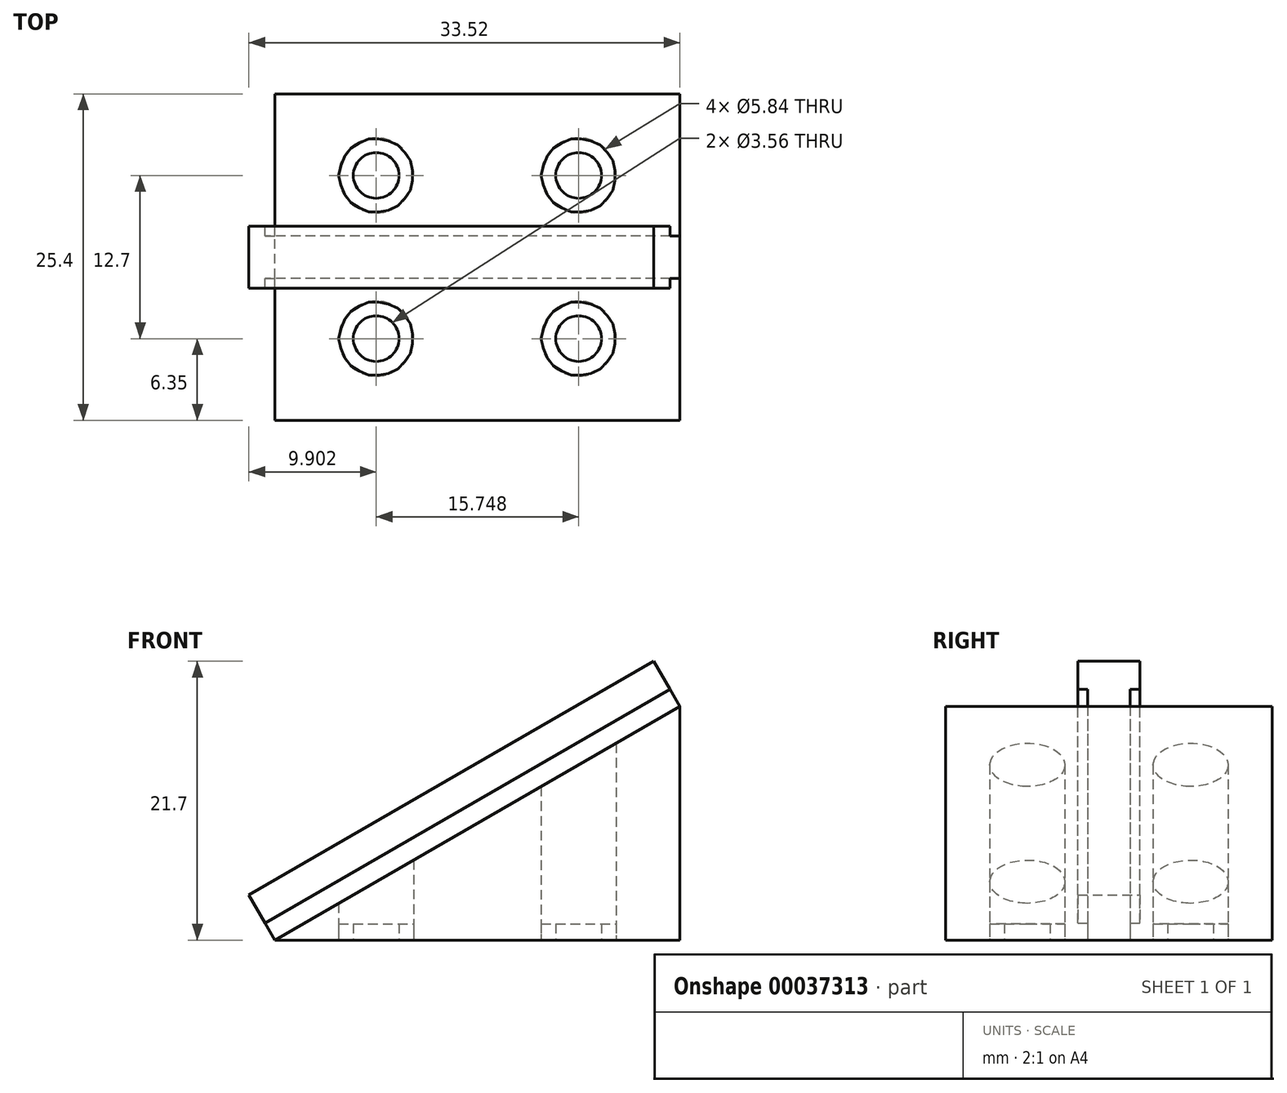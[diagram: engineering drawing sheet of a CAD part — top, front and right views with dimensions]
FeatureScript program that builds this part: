
annotation { "Feature Type Name" : "Feature", "Feature Type Description" : "" }
export const myFeature = defineFeature(function(context is Context, id is Id, definition is map)
    precondition{}
    {
        {
            var Q0;
            Q0=qCreatedBy(makeId("Front.planeOp"),FACE);
            var sketch = newSketch(context, id + "F0", { "sketchPlane" : qUnion([Q0])});
            skLineSegment(sketch, "E0", {"start": v(-14.92, 0) * mm, "end": v(16.57, 0) * mm});
            skLineSegment(sketch, "E1", {"start": v(-14.92, 0) * mm, "end": v(17.55, 18.75) * mm});
            skLineSegment(sketch, "E2", {"start": v(16.57, 0) * mm, "end": v(16.57, 18.18) * mm});
            skLineSegment(sketch, "E3", {"start": v(16.57, 18.18) * mm, "end": v(17.55, 18.75) * mm});
            skSolve(sketch);
        }
        {
            var Q0;
            Q0 = qSketchRegion(id + "F0", true);
            extrude(context, id + "F1", {"entities" : qUnion([Q0]), "depth" : 25.4 * mm});
        }
        {
            var Q0;
            Q0=makeQuery(id+"F1.opExtrude","SWEPT_FACE",FACE,{"disambiguationData":[OSD([sQuery(id+"F0.wireOp",EDGE,"E0")])]});
            var sketch = newSketch(context, id + "F2", { "sketchPlane" : qUnion([Q0])});
            skPoint(sketch, "E4.start.orphan", {"position": v(0.83, 0) * mm});
            skPoint(sketch, "E5.trimOffspring.end.orphan", {"position": v(0.83, 25.4) * mm});
            skCircle(sketch, "E6", {"center": v(-7.05, 19.05) * mm, "radius": 1.78 * mm});
            skCircle(sketch, "E7", {"center": v(-7.05, 19.05) * mm, "radius": 2.92 * mm});
            skCircle(sketch, "E8.MirrorC", {"center": v(8.7, 19.05) * mm, "radius": 1.78 * mm});
            skCircle(sketch, "E9.MirrorC", {"center": v(8.7, 19.05) * mm, "radius": 2.92 * mm});
            skPoint(sketch, "E10.orphan", {"position": v(16.57, 12.7) * mm});
            skPoint(sketch, "E11.start.orphan", {"position": v(-14.92, 12.7) * mm});
            skCircle(sketch, "E12.MirrorC", {"center": v(-7.05, 6.35) * mm, "radius": 1.78 * mm});
            skCircle(sketch, "E13.MirrorC", {"center": v(-7.05, 6.35) * mm, "radius": 2.92 * mm});
            skCircle(sketch, "E14.MirrorC", {"center": v(8.7, 6.35) * mm, "radius": 2.92 * mm});
            skCircle(sketch, "E15.MirrorC", {"center": v(8.7, 6.35) * mm, "radius": 1.78 * mm});
            skSolve(sketch);
        }
        {
            var Q0;
            Q0=makeQuery(id+"F2.imprint","IMPRINT",FACE,{"disambiguationData":[TD([[makeQuery(id+"F2.imprint","IMPRINT",EDGE,{"derivedFrom":sQuery(id+"F2.wireOp",EDGE,"E6")}),1.0]])]});
            var Q1;
            Q1=makeQuery(id+"F2.imprint","IMPRINT",FACE,{"disambiguationData":[TD([[makeQuery(id+"F2.imprint","IMPRINT",EDGE,{"derivedFrom":sQuery(id+"F2.wireOp",EDGE,"E8.MirrorC")}),-1.0]])]});
            var Q2;
            Q2=makeQuery(id+"F2.imprint","IMPRINT",FACE,{"disambiguationData":[TD([[makeQuery(id+"F2.imprint","IMPRINT",EDGE,{"derivedFrom":sQuery(id+"F2.wireOp",EDGE,"E6")}),-1.0]])]});
            var Q3;
            Q3=makeQuery(id+"F2.imprint","IMPRINT",FACE,{"disambiguationData":[TD([[makeQuery(id+"F2.imprint","IMPRINT",EDGE,{"derivedFrom":sQuery(id+"F2.wireOp",EDGE,"E8.MirrorC")}),1.0]])]});
            var Q4;
            Q4=makeQuery(id+"F2.imprint","IMPRINT",FACE,{"disambiguationData":[TD([[makeQuery(id+"F2.imprint","IMPRINT",EDGE,{"derivedFrom":sQuery(id+"F2.wireOp",EDGE,"E12.MirrorC")}),-1.0]])]});
            var Q5;
            Q5=makeQuery(id+"F2.imprint","IMPRINT",FACE,{"disambiguationData":[TD([[makeQuery(id+"F2.imprint","IMPRINT",EDGE,{"derivedFrom":sQuery(id+"F2.wireOp",EDGE,"E12.MirrorC")}),1.0]])]});
            var Q6;
            Q6=makeQuery(id+"F2.imprint","IMPRINT",FACE,{"disambiguationData":[TD([[makeQuery(id+"F2.imprint","IMPRINT",EDGE,{"derivedFrom":sQuery(id+"F2.wireOp",EDGE,"E14.MirrorC")}),1.0]])]});
            var Q7;
            Q7=makeQuery(id+"F2.imprint","IMPRINT",FACE,{"disambiguationData":[TD([[makeQuery(id+"F2.imprint","IMPRINT",EDGE,{"derivedFrom":sQuery(id+"F2.wireOp",EDGE,"E15.MirrorC")}),1.0]])]});
            extrude(context, id + "F3", {"entities" : qUnion([Q0, Q1, Q2, Q3, Q4, Q5, Q6, Q7]), "operationType" : NewBodyOperationType.REMOVE, "oppositeDirection" : true, "depth" : 25.4 * mm});
        }
        {
            var Q0;
            Q0=makeQuery(id+"F2.imprint","IMPRINT",FACE,{"disambiguationData":[TD([[makeQuery(id+"F2.imprint","IMPRINT",EDGE,{"derivedFrom":sQuery(id+"F2.wireOp",EDGE,"E6")}),-1.0]])]});
            var Q1;
            Q1=makeQuery(id+"F2.imprint","IMPRINT",FACE,{"disambiguationData":[TD([[makeQuery(id+"F2.imprint","IMPRINT",EDGE,{"derivedFrom":sQuery(id+"F2.wireOp",EDGE,"E8.MirrorC")}),1.0]])]});
            var Q2;
            Q2=makeQuery(id+"F2.imprint","IMPRINT",FACE,{"disambiguationData":[TD([[makeQuery(id+"F2.imprint","IMPRINT",EDGE,{"derivedFrom":sQuery(id+"F2.wireOp",EDGE,"E12.MirrorC")}),1.0]])]});
            var Q3;
            Q3=makeQuery(id+"F2.imprint","IMPRINT",FACE,{"disambiguationData":[TD([[makeQuery(id+"F2.imprint","IMPRINT",EDGE,{"derivedFrom":sQuery(id+"F2.wireOp",EDGE,"E14.MirrorC")}),1.0]])]});
            extrude(context, id + "F4", {"entities" : qUnion([Q0, Q1, Q2, Q3]), "oppositeDirection" : true, "depth" : 1.27 * mm});
        }
        {
            var Q0;
            Q0=makeQuery(id+"F1.opExtrude","SWEPT_FACE",FACE,{"disambiguationData":[OSD([sQuery(id+"F0.wireOp",EDGE,"E1")])]});
            var sketch = newSketch(context, id + "F5", { "sketchPlane" : qUnion([Q0])});
            skPoint(sketch, "E16", {"position": v(23.45, -14.35) * mm});
            skLineSegment(sketch, "E17", {"start": v(23.45, -14.35) * mm, "end": v(-12.92, -14.35) * mm});
            skLineSegment(sketch, "E18", {"start": v(23.45, -11.05) * mm, "end": v(-12.92, -11.05) * mm});
            skPoint(sketch, "E19.end.orphan", {"position": v(-12.92, -12.7) * mm});
            skPoint(sketch, "E19.start.orphan", {"position": v(23.45, -12.7) * mm});
            skLineSegment(sketch, "E20", {"start": v(-12.92, -14.35) * mm, "end": v(-12.92, -11.05) * mm});
            skLineSegment(sketch, "E21", {"start": v(23.45, -14.35) * mm, "end": v(23.45, -11.05) * mm});
            skSolve(sketch);
        }
        {
            var Q0;
            Q0 = qSketchRegion(id + "F5", true);
            extrude(context, id + "F6", {"entities" : qUnion([Q0]), "operationType" : NewBodyOperationType.ADD, "depth" : 1.52 * mm});
        }
        {
            var Q0;
            Q0=makeQuery(id+"F6.opExtrude","CAP_FACE",FACE,{"disambiguationData":[OSD([sQuery(id+"F5.wireOp",EDGE,"E17"),sQuery(id+"F5.wireOp",EDGE,"E18"),sQuery(id+"F5.wireOp",EDGE,"bb4d3f77-3e67-4ba7-8962-98d6ebb2e0c3"),sQuery(id+"F5.wireOp",EDGE,"E20")])],"isStart":false});
            var sketch = newSketch(context, id + "F7", { "sketchPlane" : qUnion([Q0])});
            skLineSegment(sketch, "E22", {"start": v(-12.92, -12.7) * mm, "end": v(-12.92, -10.29) * mm});
            skLineSegment(sketch, "E23", {"start": v(23.45, -12.7) * mm, "end": v(23.45, -10.29) * mm});
            skLineSegment(sketch, "E24", {"start": v(-12.92, -10.29) * mm, "end": v(23.45, -10.29) * mm});
            skLineSegment(sketch, "E25", {"start": v(23.45, -12.7) * mm, "end": v(23.45, -15.11) * mm});
            skLineSegment(sketch, "E26", {"start": v(-12.92, -12.7) * mm, "end": v(-12.92, -15.11) * mm});
            skLineSegment(sketch, "E27", {"start": v(-12.92, -15.11) * mm, "end": v(23.45, -15.11) * mm});
            skSolve(sketch);
        }
        {
            var Q0;
            Q0 = qSketchRegion(id + "F7", true);
            extrude(context, id + "F8", {"entities" : qUnion([Q0]), "operationType" : NewBodyOperationType.ADD, "depth" : 2.54 * mm});
        }
    });
